# Revit family: Hager-WITTY PLUS ON PEDESTAL-es-ES-ES
name_source: partatom
category: Electrical Fixtures
units: mm (PartAtom-declared; Revit-internal decimal feet)

## family parameters
Always vertical = Yes
Cut with Voids When Loaded = No
Maintain Annotation Orientation = No
Part Type = Normal
Room Calculation Point = No
Round Connector Dimension = Use Diameter
Shared = No
Work Plane-Based = No

## types (4) — shared parameters
BC_METADATA = {"ObjectGuid":"309c69a2-f6b5-4723-8d44-322179afe64e","ModelGuid":"04826155-e6fb-4358-826f-cf700e871803","VariantGuid":"d0dc6e8a-84e1-41b3-adf0-62c97217fd0d","Revision":"#2","VariantName":"REF 1"}
BC_MODEL_ID = 1528361
BC_OBJECT_ID = 511110
BC_OBJECT_VERSION = #1
Code hager = ADD_EC002883_ECVS_WO
EF000003 - Método de montaje = Montaje en pared
EF000008 - Anchura = 250 mm  [stored 0.82021 ft]
EF000040 - Altura = 370 mm  [stored 1.21391 ft]
EF000049 - Profundidad = 150 mm
EF000458 - Con pantalla = No
EF001596 - Material de carcasa = Plástico
EF002136 - Potencia nominal de entrada = 22000 W
EF003840 - Tensión de entrada = 400 V
EF004293 - Resistencia al impacto (IK) = IK10
EF005455 - Frecuencia = 50/60 Hz
EF005474 - Grado de protección (IP) = IP55
EF007001 - Voltaje de salida en CC = 0 V
EF007353 - Corriente máx. de salida CC = 0 A
EF009078 - Número de puntos de carga = 1
EF009089 - Con caja de distribución eléctrica = No
EF009300 - Potencia máx. por punto de carga = 22000 W
EF009305 - Número de enchufes de carga tipo 2 = 1
EF009313 - Con medido de energía = Yes
EF009314 - Con disyuntor de protección = No
EF009547 - LTE = No
EF011072 - Compatible IFTTT = No
EF012191 - Con lector de tarjetas RFID integrado = Yes
EF012361 - NFC (Near Field Communication) = No
EF013154 - Conexión a través de WiFi = Yes
EF014925 - Compatible con Apple HomeKit = No
EF014926 - Compatible con Google Assistant = No
EF014927 - Compatible con Amazon Alexa = No
EF016385 - Estándar de radio 5G = No
EF017508 - Conectable a la red como maestro = No
EF017509 - Detección de corriente residual CC = No
EF017511 - Con interruptor de llave = No
EF017512 - Exportación de registros de carga = Yes
EF017513 - Versión del protocolo de punto de carga abierto (OCPP) = 1.6
EF017515 - Enchufar y cargar (ISO 15118) = No
EF017517 - Conectable a la red como extensor = No
EF017663 - Cable de carga bloqueable en el dispositivo de carga = No
EF017664 - Conexión de red a través de LAN = Yes
EF017665 - Con contador de energía compatible con MID = Yes
EF017668 - Gestión de carga estática integrada = No
EF017669 - Apto para la gestión de carga dinámica = Yes
EF017672 - Back-end integrado = No
EF017972 - Funcionamiento y configuración por app = Yes
EF025053 - Ejecución de la conexión en el lado de la instalación = Trifásico
EFDE0066 - Conforme a la ley de calibración = No
ETIM class code = EC002883
ETIM class name = Charging device E-Mobility
HG000003-Range = WITTY PLUS
HG000065-With socket TE = No
HG000099-Onfly Template ID = WittyOne_EVCS_On_Pedestal
Manufacturer = hager France
Name = WITTY PLUS ON PEDESTAL-ES
Name BIM&CO = Electricity
Name hager = ADD_ChargingStation_EC002883
Reference description = ECVS Witty 1x22kW 3P T2S
zero-valued in all types: Default Elevation, EF006577 - Número de tomas de corriente CEE, EF008200 - Sección transversal del conductor conectable, EF009091 - Número de interruptores diferenciales tipo A, EF009092 - Número de interruptores diferenciales tipo B, EF009301 - Número de conectores de carga tipo 1, EF009302 - Número de conectores de carga tipo 1 CCS, EF009303 - Número de conectores de carga tipo 2, EF009304 - Número de conectores de carga tipo 2 CCS, EF009306 - Número de conectores de carga GB CA, EF009307 - Número de conectores de carga GB CC, EF009308 - Número de enchufes de carga tipo GB, EF009309 - Número de enchufes de carga tipo 3, EF009310 - Número de conectores de carga CHAdeMO, EF009311 - Número de enchufes domésticos

## per-type parameters (varying)
| type | BC_VARIANT_ID | EF014895 - Longitud del cable de carga | HG000004-Manufacturer reference |
| WITTY PLUS-1x22kW-3P-XVL122C-RECTANGULAR PEDESTAL | 1164440 | 6500 mm  [stored 21.3255 ft] | XVL122C / XVA130 |
| WITTY PLUS-1x22kW-3P-XVL122C-DOUBLE STATION-RECTANGULAR PEDESTAL | 1164442 | 6500 mm  [stored 21.3255 ft] | XVL122C / XVL122C / XVA135 |
| WITTY PLUS-1x22kW-3P-XVL122S-DOUBLE STATION-RECTANGULAR PEDESTAL | 1164443 | 0 mm  [stored 0 ft] | XVL122S / XVL122S / XVA135 |
| WITTY PLUS-1x22kW-3P-XVL122S-RECTANGULAR PEDESTAL | 1164445 | 0 mm  [stored 0 ft] | XVL122S / XVA130 |

note: column(s) folded — value = type name in every type: Reference

note: [stored X ft] marks values corroborated as IEEE doubles in the binary element streams (Revit-internal decimal feet)
